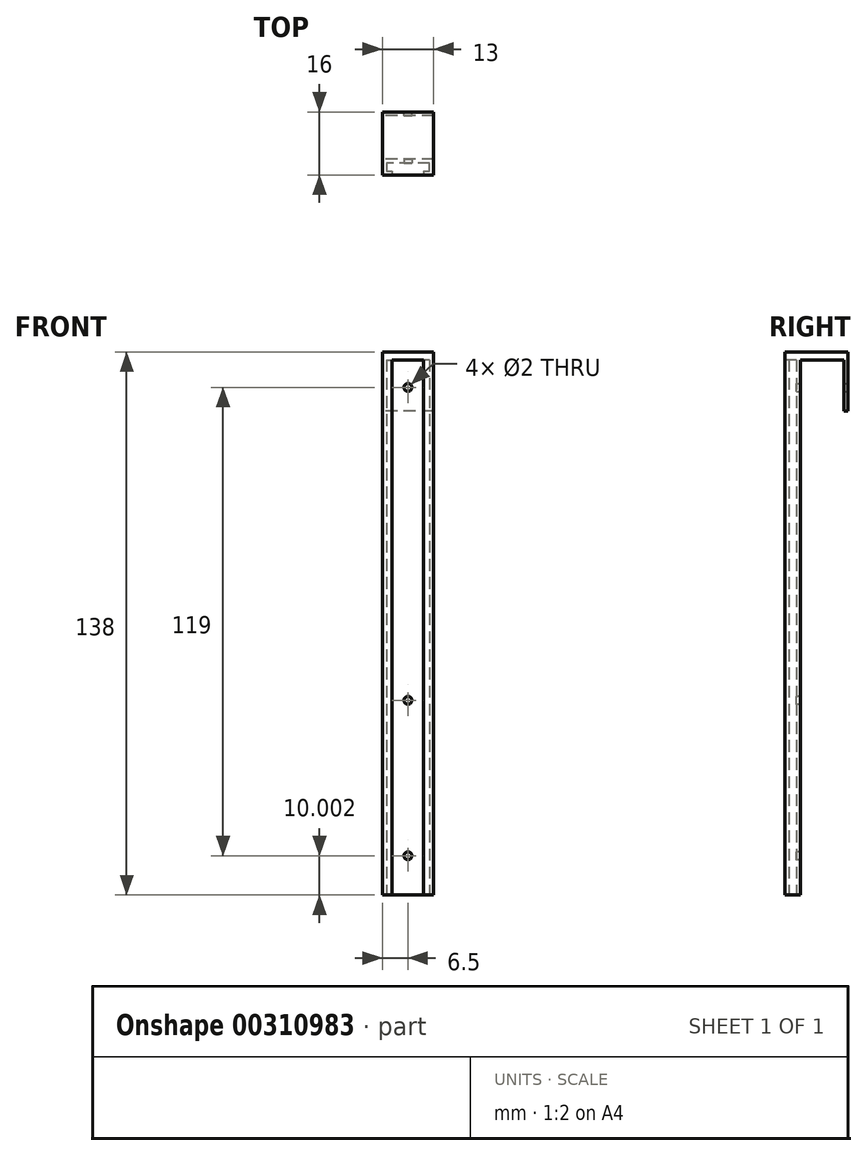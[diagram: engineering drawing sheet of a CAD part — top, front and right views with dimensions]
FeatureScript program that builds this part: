
annotation { "Feature Type Name" : "Feature", "Feature Type Description" : "" }
export const myFeature = defineFeature(function(context is Context, id is Id, definition is map)
    precondition{}
    {
        {
            var Q0;
            Q0=qCreatedBy(makeId("Front.planeOp"),FACE);
            var sketch = newSketch(context, id + "F0", { "sketchPlane" : qUnion([Q0])});
            skLineSegment(sketch, "E0", {"start": v(-6.5, -56.2) * mm, "end": v(-6.5, 81.8) * mm});
            skLineSegment(sketch, "E1", {"start": v(-6.5, 81.8) * mm, "end": v(6.5, 81.8) * mm});
            skLineSegment(sketch, "E2", {"start": v(6.5, 81.8) * mm, "end": v(6.5, -56.2) * mm});
            skLineSegment(sketch, "E3", {"start": v(-6.5, -56.2) * mm, "end": v(6.5, -56.2) * mm});
            skSolve(sketch);
        }
        {
            var Q0;
            Q0=makeQuery(id+"F0.imprint","IMPRINT",FACE,{"disambiguationData":[TD([[makeQuery(id+"F0.imprint","IMPRINT",EDGE,{"derivedFrom":sQuery(id+"F0.wireOp",EDGE,"E0")}),-1.0]])]});
            extrude(context, id + "F1", {"entities" : qUnion([Q0]), "depth" : 4 * mm});
        }
        {
            var Q0;
            Q0=makeQuery(id+"F1.opExtrude","SWEPT_FACE",FACE,{"disambiguationData":[OSD([sQuery(id+"F0.wireOp",EDGE,"E3")])]});
            var sketch = newSketch(context, id + "F2", { "sketchPlane" : qUnion([Q0])});
            skLineSegment(sketch, "E4", {"start": v(-4, 0) * mm, "end": v(-4, 1) * mm});
            skLineSegment(sketch, "E5", {"start": v(-4, 1) * mm, "end": v(-5.5, 1) * mm});
            skLineSegment(sketch, "E6", {"start": v(-5.5, 1) * mm, "end": v(-5.5, 3) * mm});
            skLineSegment(sketch, "E7", {"start": v(-5.5, 3) * mm, "end": v(5.5, 3) * mm});
            skLineSegment(sketch, "E8", {"start": v(5.5, 3) * mm, "end": v(5.5, 1) * mm});
            skLineSegment(sketch, "E9", {"start": v(5.5, 1) * mm, "end": v(4, 1) * mm});
            skLineSegment(sketch, "E10", {"start": v(4, 1) * mm, "end": v(4, 0) * mm});
            skLineSegment(sketch, "E11", {"start": v(4, 0) * mm, "end": v(6.5, 0) * mm});
            skLineSegment(sketch, "E12", {"start": v(6.5, 0) * mm, "end": v(6.5, 4) * mm});
            skLineSegment(sketch, "E13", {"start": v(6.5, 4) * mm, "end": v(-6.5, 4) * mm});
            skLineSegment(sketch, "E14", {"start": v(-6.5, 4) * mm, "end": v(-6.5, 0) * mm});
            skLineSegment(sketch, "E15", {"start": v(-6.5, 0) * mm, "end": v(-4, 0) * mm});
            skLineSegment(sketch, "E16", {"start": v(-4, 1) * mm, "end": v(4, 1) * mm});
            skLineSegment(sketch, "E17", {"start": v(4, 3) * mm, "end": v(4, 4) * mm});
            skLineSegment(sketch, "E18", {"start": v(-4, 3) * mm, "end": v(-4, 4) * mm});
            skSolve(sketch);
        }
        {
            var Q0;
            {var subQ0=sQuery(id+"F2.wireOp",EDGE,"E17");Q0=makeQuery(id+"F2.imprint","IMPRINT",FACE,{"disambiguationData":[TD([[makeQuery(id+"F2.imprint","IMPRINT",EDGE,{"derivedFrom":subQ0}),1.0]])]});}
            var Q1;
            Q1=makeQuery(id+"F2.imprint","IMPRINT",FACE,{"disambiguationData":[TD([[makeQuery(id+"F2.imprint","IMPRINT",EDGE,{"derivedFrom":sQuery(id+"F2.wireOp",EDGE,"E5")}),-1.0]])]});
            extrude(context, id + "F3", {"entities" : qUnion([Q0, Q1]), "operationType" : NewBodyOperationType.REMOVE, "oppositeDirection" : true, "depth" : 136 * mm});
        }
        {
            var Q0;
            Q0=makeQuery(id+"F1.opExtrude","CAP_FACE",FACE,{"disambiguationData":[OSD([sQuery(id+"F0.wireOp",EDGE,"E0"),sQuery(id+"F0.wireOp",EDGE,"E1"),sQuery(id+"F0.wireOp",EDGE,"E2"),sQuery(id+"F0.wireOp",EDGE,"E3")])],"isStart":false});
            var sketch = newSketch(context, id + "F4", { "sketchPlane" : qUnion([Q0])});
            skCircle(sketch, "E19", {"center": v(0, -46.2) * mm, "radius": 1 * mm});
            skSolve(sketch);
        }
        {
            var Q0;
            Q0=makeQuery(id+"F4.imprint","IMPRINT",FACE,{"disambiguationData":[TD([[makeQuery(id+"F4.imprint","IMPRINT",EDGE,{"derivedFrom":sQuery(id+"F4.wireOp",EDGE,"E19")}),1.0]])]});
            extrude(context, id + "F5", {"entities" : qUnion([Q0]), "operationType" : NewBodyOperationType.REMOVE, "endBound" : BoundingType.THROUGH_ALL, "oppositeDirection" : true, "depth" : 25 * mm});
        }
        {
            var Q0;
            Q0=makeQuery(id+"F1.opExtrude","CAP_FACE",FACE,{"disambiguationData":[OSD([sQuery(id+"F0.wireOp",EDGE,"E0"),sQuery(id+"F0.wireOp",EDGE,"E1"),sQuery(id+"F0.wireOp",EDGE,"E2"),sQuery(id+"F0.wireOp",EDGE,"E3")])],"isStart":false});
            var sketch = newSketch(context, id + "F6", { "sketchPlane" : qUnion([Q0])});
            skCircle(sketch, "E20", {"center": v(0, -6.7) * mm, "radius": 1 * mm});
            skSolve(sketch);
        }
        {
            var Q0;
            Q0=makeQuery(id+"F6.imprint","IMPRINT",FACE,{"disambiguationData":[TD([[makeQuery(id+"F6.imprint","IMPRINT",EDGE,{"derivedFrom":sQuery(id+"F6.wireOp",EDGE,"E20")}),1.0]])]});
            extrude(context, id + "F7", {"entities" : qUnion([Q0]), "operationType" : NewBodyOperationType.REMOVE, "endBound" : BoundingType.THROUGH_ALL, "oppositeDirection" : true, "depth" : 25 * mm});
        }
        {
            var Q0;
            Q0=makeQuery(id+"F1.opExtrude","CAP_FACE",FACE,{"disambiguationData":[OSD([sQuery(id+"F0.wireOp",EDGE,"E0"),sQuery(id+"F0.wireOp",EDGE,"E1"),sQuery(id+"F0.wireOp",EDGE,"E2"),sQuery(id+"F0.wireOp",EDGE,"E3")])],"isStart":true});
            var sketch = newSketch(context, id + "F8", { "sketchPlane" : qUnion([Q0])});
            skLineSegment(sketch, "E21.bottom", {"start": v(-6.5, 81.8) * mm, "end": v(6.5, 81.8) * mm});
            skLineSegment(sketch, "E21.top", {"start": v(-6.5, 79.8) * mm, "end": v(6.5, 79.8) * mm});
            skLineSegment(sketch, "E21.left", {"start": v(-6.5, 81.8) * mm, "end": v(-6.5, 79.8) * mm});
            skLineSegment(sketch, "E21.right", {"start": v(6.5, 81.8) * mm, "end": v(6.5, 79.8) * mm});
            skSolve(sketch);
        }
        {
            var Q0;
            Q0=makeQuery(id+"F8.imprint","IMPRINT",FACE,{"disambiguationData":[TD([[makeQuery(id+"F8.imprint","IMPRINT",EDGE,{"derivedFrom":sQuery(id+"F8.wireOp",EDGE,"E21.bottom")}),1.0]])]});
            extrude(context, id + "F9", {"entities" : qUnion([Q0]), "operationType" : NewBodyOperationType.ADD, "depth" : 12 * mm});
        }
        {
            var Q0;
            Q0=makeQuery(id+"F9.opExtrude","SWEPT_FACE",FACE,{"disambiguationData":[OSD([sQuery(id+"F8.wireOp",EDGE,"E21.top")])]});
            var sketch = newSketch(context, id + "F10", { "sketchPlane" : qUnion([Q0])});
            skLineSegment(sketch, "E22.bottom", {"start": v(6.5, -12) * mm, "end": v(-6.5, -12) * mm});
            skLineSegment(sketch, "E22.top", {"start": v(6.5, -11) * mm, "end": v(-6.5, -11) * mm});
            skLineSegment(sketch, "E22.left", {"start": v(6.5, -12) * mm, "end": v(6.5, -11) * mm});
            skLineSegment(sketch, "E22.right", {"start": v(-6.5, -12) * mm, "end": v(-6.5, -11) * mm});
            skSolve(sketch);
        }
        {
            var Q0;
            Q0=makeQuery(id+"F10.imprint","IMPRINT",FACE,{"disambiguationData":[TD([[makeQuery(id+"F10.imprint","IMPRINT",EDGE,{"derivedFrom":sQuery(id+"F10.wireOp",EDGE,"E22.bottom")}),-1.0]])]});
            extrude(context, id + "F11", {"entities" : qUnion([Q0]), "operationType" : NewBodyOperationType.ADD, "depth" : 13 * mm});
        }
        {
            var Q0;
            Q0=makeQuery(id+"FtlNNAsC0BUfwGC_1.boolean.opBoolean","MERGE",FACE,{"derivedFrom":[makeQuery(id+"F9.opExtrude","CAP_FACE",FACE,{"disambiguationData":[OSD([sQuery(id+"F8.wireOp",EDGE,"E21.bottom"),sQuery(id+"F8.wireOp",EDGE,"E21.top"),sQuery(id+"F8.wireOp",EDGE,"E21.left"),sQuery(id+"F8.wireOp",EDGE,"E21.right")])],"isStart":false}),makeQuery(id+"FtlNNAsC0BUfwGC_1.opExtrude","SWEPT_FACE",FACE,{"disambiguationData":[OSD([sQuery(id+"FPEhc0m82GioeeF_1.wireOp",EDGE,"UxWwKRRH-LqVb-Rd6p-vtS6-PNJbk1hAGm2Y.bottom")])]})]});
            var sketch = newSketch(context, id + "F12", { "sketchPlane" : qUnion([Q0])});
            skCircle(sketch, "E23", {"center": v(0, 72.8) * mm, "radius": 1 * mm});
            skSolve(sketch);
        }
        {
            var Q0;
            Q0=makeQuery(id+"F12.imprint","IMPRINT",FACE,{"disambiguationData":[TD([[makeQuery(id+"F12.imprint","IMPRINT",EDGE,{"derivedFrom":sQuery(id+"F12.wireOp",EDGE,"E23")}),1.0]])]});
            extrude(context, id + "F13", {"entities" : qUnion([Q0]), "operationType" : NewBodyOperationType.REMOVE, "endBound" : BoundingType.THROUGH_ALL, "oppositeDirection" : true, "depth" : 25 * mm});
        }
    });
